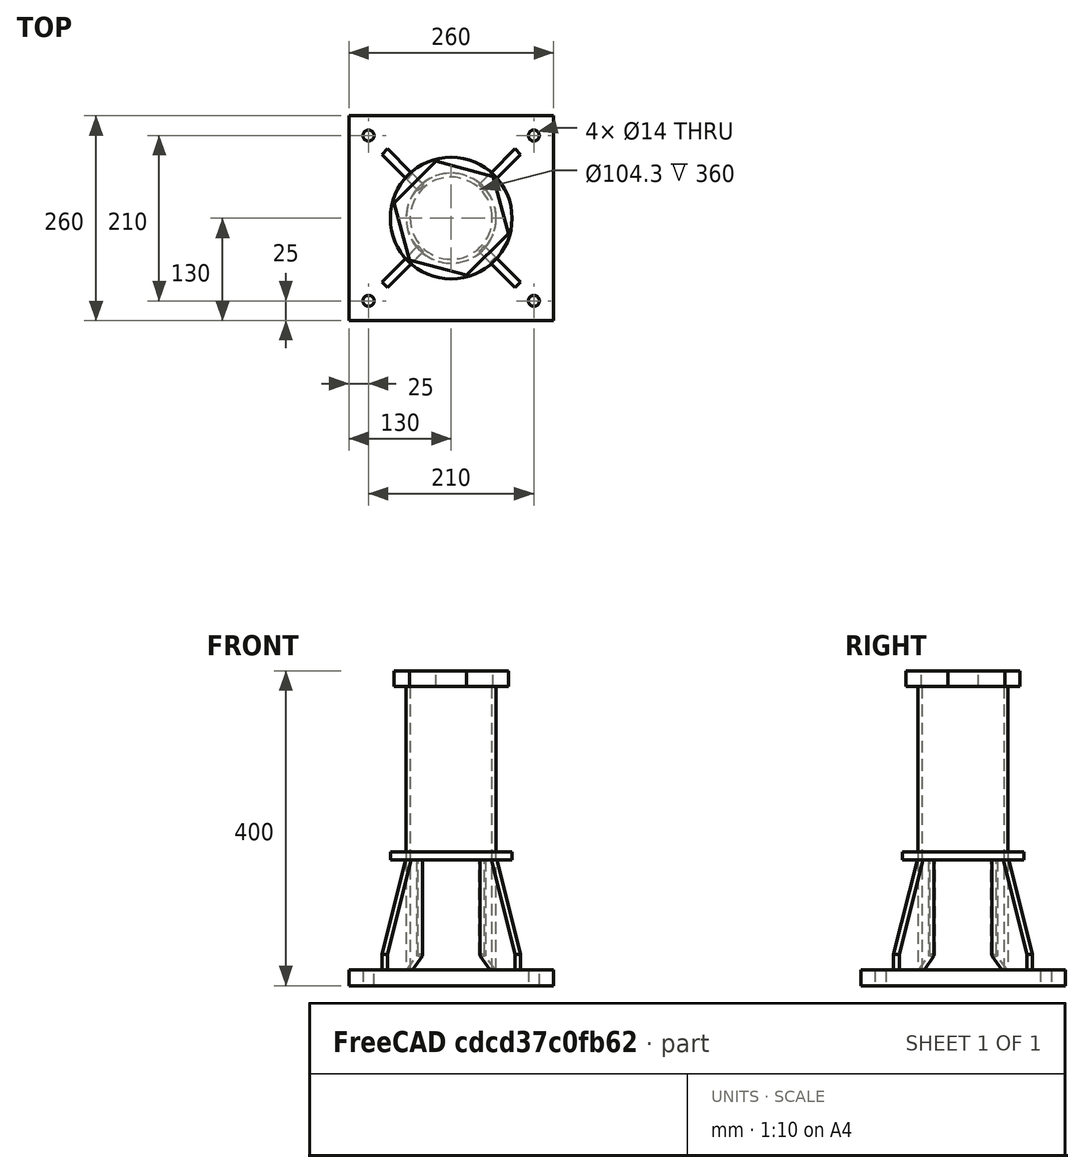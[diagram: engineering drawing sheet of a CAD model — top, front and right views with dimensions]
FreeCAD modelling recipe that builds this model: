
FCSTD DOCUMENT  (FreeCAD 0.21R33771 (Git))
Label: Wyk_Rohrstoss_ring
License: All rights reserved
LicenseURL: http://en.wikipedia.org/wiki/All_rights_reserved
objects: Sketcher::SketchObject×4, Part::Extrusion×4, Part::FeaturePython×3, Fem::ConstraintForce×3, Fem::FemSolverObjectPython×1, App::MaterialObjectPython×1, Part::Revolution×1, Fem::ConstraintFixed×1, Fem::FemMeshObjectPython×1, Fem::FemAnalysis×1
note: 12 computed .brp shape members not serialized (recipe doc carries the construction recipe); baked Part::Feature solids carry a one-line shape summary decoded from their .brp

FEATURE [Sketcher::SketchObject] Sketch
  FullyConstrained = true
  sketch-geometry (12):
    g0: LineSegment StartX=-130 StartY=130 StartZ=0 EndX=130 EndY=130 EndZ=0
    g1: LineSegment StartX=130 StartY=130 StartZ=0 EndX=130 EndY=-130 EndZ=0
    g2: LineSegment StartX=130 StartY=-130 StartZ=0 EndX=-130 EndY=-130 EndZ=0
    g3: LineSegment StartX=-130 StartY=-130 StartZ=0 EndX=-130 EndY=130 EndZ=0
    g4: LineSegment StartX=-105 StartY=105 StartZ=0 EndX=105 EndY=105 EndZ=0
    g5: LineSegment StartX=105 StartY=105 StartZ=0 EndX=105 EndY=-105 EndZ=0
    g6: LineSegment StartX=105 StartY=-105 StartZ=0 EndX=-105 EndY=-105 EndZ=0
    g7: LineSegment StartX=-105 StartY=-105 StartZ=0 EndX=-105 EndY=105 EndZ=0
    g8: Circle CenterX=-105 CenterY=105 CenterZ=0 NormalX=0 NormalY=0 NormalZ=1 AngleXU=0 Radius=7
    g9: Circle CenterX=105 CenterY=105 CenterZ=0 NormalX=0 NormalY=0 NormalZ=1 AngleXU=0 Radius=7
    g10: Circle CenterX=-105 CenterY=-105 CenterZ=0 NormalX=0 NormalY=0 NormalZ=1 AngleXU=0 Radius=7
    g11: Circle CenterX=105 CenterY=-105 CenterZ=0 NormalX=0 NormalY=0 NormalZ=1 AngleXU=0 Radius=7
  constraints (28):
    c: Coincident(g0,g1)
    c: Coincident(g1,g2)
    c: Coincident(g2,g3)
    c: Coincident(g3,g0)
    c: Horizontal(g0)
    c: Vertical(g1)
    c: Symmetric(g2,g1,g-2)
    c: Symmetric(g2,g0,g-1)
    c: Equal(g2,g3)
    c: DistanceX(g2,g2) = 260
    c: Coincident(g4,g5)
    c: Coincident(g5,g6)
    c: Coincident(g6,g7)
    c: Coincident(g7,g4)
    c: Horizontal(g4)
    c: Vertical(g7)
    c: Symmetric(g5,g4,g-1)
    c: Symmetric(g6,g5,g-2)
    c: Equal(g6,g5)
    c: DistanceX(g6,g6) = 210
    c: Coincident(g8,g4)
    c: Coincident(g9,g4)
    c: Coincident(g10,g6)
    c: Coincident(g11,g5)
    c: Equal(g8,g9)
    c: Equal(g8,g11)
    c: Equal(g8,g10)
    c: Diameter(g8) = 14
FEATURE [Part::Extrusion] Extrude  label="platte"
  Base = -> Sketch
  Dir = (0,0,1)
  DirMode = 2
  FaceMakerClass = Part::FaceMakerBullseye
  LengthFwd = 20
  LengthRev = 0
  Solid = true
  Symmetric = false
FEATURE [Sketcher::SketchObject] Sketch001
  FullyConstrained = true
  MapMode = 5
  Placement = pos=(0,0,20) rot=(0,0,1;0rad)
  Support = -> [Extrude]
  sketch-geometry (3):
    g0: Circle CenterX=0 CenterY=0 CenterZ=0 NormalX=0 NormalY=0 NormalZ=1 AngleXU=0 Radius=57.15
    g1: Circle CenterX=0 CenterY=0 CenterZ=0 NormalX=0 NormalY=0 NormalZ=1 AngleXU=0 Radius=52.15
    g2: LineSegment StartX=52.15 StartY=0 StartZ=0 EndX=57.15 EndY=0 EndZ=0
  constraints (8):
    c: Coincident(g0,g-1)
    c: Coincident(g1,g0)
    c: Diameter(g0) = 114.3
    c: PointOnObject(g2,g1)
    c: PointOnObject(g2,g0)
    c: PointOnObject(g2,g-1)
    c: Horizontal(g2)
    c: DistanceX(g2,g2) = 5
FEATURE [Part::Extrusion] Extrude001  label="R114x5"
  Base = -> Sketch001
  Dir = (0,0,1)
  DirMode = 2
  FaceMakerClass = Part::FaceMakerBullseye
  LengthFwd = 360
  LengthRev = 0
  Solid = true
  Symmetric = false
FEATURE [Sketcher::SketchObject] Sketch002
  ExternalGeometry = -> [Extrude]
  FullyConstrained = true
  Placement = pos=(0,0,0) rot=(1,0,0;1.5708rad)
  sketch-geometry (6):
    g0: LineSegment StartX=54.65 StartY=160 StartZ=0 EndX=77.15 EndY=160 EndZ=0
    g1: LineSegment StartX=77.15 StartY=160 StartZ=0 EndX=119.65 EndY=40 EndZ=0
    g2: LineSegment StartX=119.65 StartY=40 StartZ=0 EndX=119.65 EndY=20 EndZ=0
    g3: LineSegment StartX=119.65 StartY=20 StartZ=0 EndX=74.65 EndY=20 EndZ=0
    g4: LineSegment StartX=74.65 StartY=20 StartZ=0 EndX=54.65 EndY=40 EndZ=0
    g5: LineSegment StartX=54.65 StartY=40 StartZ=0 EndX=54.65 EndY=160 EndZ=0
  constraints (18):
    c: Horizontal(g0)
    c: Coincident(g0,g1)
    c: Coincident(g1,g2)
    c: Vertical(g2)
    c: Coincident(g2,g3)
    c: Coincident(g3,g4)
    c: Coincident(g4,g5)
    c: Coincident(g5,g0)
    c: Vertical(g5)
    c: Horizontal(g3)
    c: Horizontal(g2,g-3)
    c: DistanceY(g3,g4) = 20
    c: DistanceX(g4,g3) = 20
    c: DistanceX(g4,g2) = 65
    c: DistanceY(g2,g2) = 20
    c: DistanceX(g-1,g4) = 54.65
    c: DistanceX(g0,g0) = 22.5
    c: DistanceY(g2,g0) = 140
FEATURE [Part::Extrusion] Extrude002
  Base = -> Sketch002
  Dir = (0,-1,2e-16)
  DirMode = 2
  FaceMakerClass = Part::FaceMakerBullseye
  LengthFwd = 10
  LengthRev = 0
  Solid = true
  Symmetric = true
FEATURE [Part::FeaturePython] Array  label="steifen"  # Draft array (typed FeaturePython)
  Angle = 360
  ArrayType = 1
  Axis = (0,0,1)
  Base = -> Extrude002
  Center = (0,0,0)
  Count = 4
  Fuse = false
  IntervalAxis = (0,0,0)
  IntervalX = (50,0,0)
  IntervalY = (0,50,0)
  IntervalZ = (0,0,50)
  NumberCircles = 3
  NumberPolar = 4
  NumberX = 2
  NumberY = 2
  NumberZ = 1
  Placement = pos=(0,0,0) rot=(0,0,1;0.785398rad)
  RadialDistance = 50
  Symmetry = 1
  TangentialDistance = 25
FEATURE [Sketcher::SketchObject] Sketch003
  FullyConstrained = true
  MapMode = 5
  Placement = pos=(0,0,380) rot=(0,0,1;0rad)
  Support = -> [Extrude001]
  sketch-geometry (8):
    g0: LineSegment StartX=72.4981 StartY=-19.4258 StartZ=0 EndX=53.0723 EndY=53.0723 EndZ=0
    g1: LineSegment StartX=53.0723 StartY=53.0723 StartZ=0 EndX=-19.4258 EndY=72.4981 EndZ=0
    g2: LineSegment StartX=-19.4258 StartY=72.4981 StartZ=0 EndX=-72.4981 EndY=19.4258 EndZ=0
    g3: LineSegment StartX=-72.4981 StartY=19.4258 StartZ=0 EndX=-53.0723 EndY=-53.0723 EndZ=0
    g4: LineSegment StartX=-53.0723 StartY=-53.0723 StartZ=0 EndX=19.4258 EndY=-72.4981 EndZ=0
    g5: LineSegment StartX=19.4258 StartY=-72.4981 StartZ=0 EndX=72.4981 EndY=-19.4258 EndZ=0
    g6: Circle CenterX=0 CenterY=0 CenterZ=0 NormalX=0 NormalY=0 NormalZ=1 AngleXU=0 Radius=75.0555
    g7: LineSegment StartX=0 StartY=0 StartZ=0 EndX=45.9619 EndY=-45.9619 EndZ=0
  constraints (18):
    c: Coincident(g0,g1)
    c: Coincident(g1,g2)
    c: Coincident(g2,g3)
    c: Coincident(g3,g4)
    c: Coincident(g4,g5)
    c: Coincident(g5,g0)
    c: Equal(g0, g1-g5) x5
    c: PointOnObject(g0,g6)
    c: PointOnObject(g1,g6)
    c: PointOnObject(g2,g6)
    c: PointOnObject(g3,g6)
    c: PointOnObject(g4,g6)
    c: Coincident(g6,g-1)
    c: Coincident(g7,g6)
    c: PointOnObject(g7,g5)
    c: Symmetric(g4,g0,g7)
    c: Angle(g7,g-1) = 0.785398
    c: Distance(g1,g0) = 130
FEATURE [Part::Extrusion] Extrude003  label="lastplatte"
  Base = -> Sketch003
  Dir = (0,0,1)
  DirMode = 2
  FaceMakerClass = Part::FaceMakerBullseye
  LengthFwd = 20
  LengthRev = 0
  Solid = true
  Symmetric = false
FEATURE [Fem::FemSolverObjectPython] SolverCcxTools  # FEM object (typed FeaturePython)
  AnalysisType = 0
  BeamShellResultOutput3D = true
  BucklingFactors = 1
  EigenmodeHighLimit = 1000000
  EigenmodeLowLimit = 0
  EigenmodesCount = 10
  GeometricalNonlinearity = 0
  IterationsControlParameterCutb = 0.25,0.5,0.75,0.85,,,1.5,
  IterationsControlParameterIter = 4,8,9,200,10,400,,200,,
  IterationsControlParameterTimeUse = false
  IterationsThermoMechMaximum = 2000
  IterationsUserDefinedIncrementations = false
  IterationsUserDefinedTimeStepLength = false
  MaterialNonlinearity = 0
  MatrixSolverType = 1
  SplitInputWriter = true
  ThermoMechSteadyState = true
  TimeEnd = 1
  TimeInitialStep = 0.01
FEATURE [App::MaterialObjectPython] MaterialSolid  label="S235"  # material (typed FeaturePython)
  Category = 0
  Material = AuthorAndLicense=(c) 2013 Juergen Riegel (CC-BY 3.0),CardName=CalculiX-Steel,Density=7900 kg/m^3,+8 more (map truncated)
FEATURE [Part::FeaturePython] Facebinder001  # WARN: FeaturePython — macro-defined, semantics opaque (R4)
  Area = 202.191
  Extrusion = 0
  RemoveSplitter = false
  Sew = false
FEATURE [Part::Revolution] Revolve
  Angle = 360
  Axis = (0,0,1)
  Base = (0,0,0)
  FaceMakerClass = Part::FaceMakerBullseye
  Solid = false
  Source = -> Facebinder001
  Symmetric = false
FEATURE [Part::FeaturePython] BooleanFragments  # WARN: FeaturePython — macro-defined, semantics opaque (R4)
  Mode = 2
  Objects = -> [Extrude,Extrude001,Array,Extrude003,Revolve]
  Tolerance = 0
FEATURE [Fem::ConstraintFixed] ConstraintFixed
  NormalDirection = (1,-1e-16,0)
  Normals = (48) [(-1,0,0),(0.5,-0.866025,0),(0.5,0.866025,0),(-1,2.44929e-16,0),(-1,0,0),(0.5,-0.866025,0),(0.5,0.866025,0),(-1,2.44929e-16,0),(-1,0,0),+39 more]
  Points = (48) [(112,105,20),(101.5,111.062,20),(101.5,98.9378,20),(112,105,20),(112,105,10),(101.5,111.062,10),(101.5,98.9378,10),(112,105,10),(112,105,0),+39 more]
  References = -> [BooleanFragments]
  Scale = 4
FEATURE [Fem::ConstraintForce] ConstraintForce
  Direction = -> BooleanFragments [Edge112]
  DirectionVector = (0,0,1)
  Force = 65330
  NormalDirection = (-0.707107,0.707107,0)
  Points = (12) [(-19.4258,72.4981,400),(-37.1166,54.8073,400),(-54.8073,37.1166,400),(-72.4981,19.4258,400),(-19.4258,72.4981,390),(-37.1166,54.8073,390),+6 more]
  References = -> [BooleanFragments]
  Scale = 6
FEATURE [Fem::ConstraintForce] ConstraintForce001
  Direction = -> BooleanFragments [Edge118]
  DirectionVector = (0,0,-1)
  Force = 65330
  NormalDirection = (0.707107,-0.707107,0)
  Points = (12) [(19.4258,-72.4981,400),(37.1166,-54.8073,400),(54.8073,-37.1166,400),(72.4981,-19.4258,400),(19.4258,-72.4981,390),(37.1166,-54.8073,390),+6 more]
  References = -> [BooleanFragments]
  Reversed = true
  Scale = 6
FEATURE [Fem::ConstraintForce] ConstraintForce002
  Direction = -> BooleanFragments [Edge33]
  DirectionVector = (0.707107,-0.707107,0)
  Force = 4410
  NormalDirection = (0,0,1)
  Points = (4) [(24.166,-24.166,400),(24.166,24.166,400),(-24.166,-24.166,400),(-24.166,24.166,400)]
  References = -> [BooleanFragments]
  Scale = 12
FEATURE [Fem::FemMeshObjectPython] FEMMeshGmsh  # FEM object (typed FeaturePython)
  Algorithm2D = 0
  Algorithm3D = 0
  CharacteristicLengthMax = 8
  CharacteristicLengthMin = 0
  CoherenceMesh = true
  ElementDimension = 0
  ElementOrder = 1
  GeometryTolerance = 1e-06
  GroupsOfNodes = false
  HighOrderOptimize = 0
  MeshSizeFromCurvature = 12
  OptimizeNetgen = false
  OptimizeStd = true
  Part = -> BooleanFragments
  RecombinationAlgorithm = 0
  Recombine3DAll = false
  RecombineAll = false
  SecondOrderLinear = false
FEATURE [Fem::FemAnalysis] Analysis
  Group = -> [SolverCcxTools,MaterialSolid,ConstraintFixed,ConstraintForce,ConstraintForce001,ConstraintForce002,FEMMeshGmsh]
